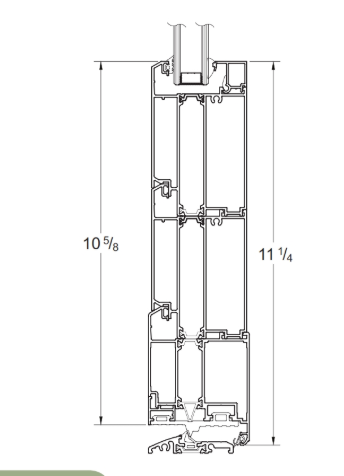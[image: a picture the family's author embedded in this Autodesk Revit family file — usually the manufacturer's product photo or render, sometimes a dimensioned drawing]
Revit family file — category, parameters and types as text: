
# Revit family: Door-Swinging-All_Weather-Series_7000-Nail_On-Outswing_Sidelite
name_source: partatom
category: Doors
units: mm (PartAtom-declared; Revit-internal decimal feet)

## family parameters
Always vertical = Yes
Classification Number = 23.30.10.00
Cut with Voids When Loaded = No
Host = Wall
Room Calculation Point = No
Shared = No

## types (4) — shared parameters
Analytic Construction = <None>
Assembly Code = B2030100
Description = 3 1/4 in frames with mitered corners
Door Width = 3' - 0"
Exterior Trim Finish = Metal-Aluminum-All_Weather-Standard-White
Exterior Trim by others = No
Finish = Metal-Aluminum-All_Weather-Standard-White
Function = Exterior
Glazing = Glass-All_Weather-OA-Insulated_Glass
Height = 8' - 0"
Inset = 0' - 0"
Interior Trim  by others = No
Interior Trim Finish = Metal-Aluminum-All_Weather-Standard-White
Jamb Ext Finish = Metal-Aluminum-All_Weather-Standard-White
Jamb Extensions = No
Manufacturer = All Weather Architectural Aluminum
Max Door Width = 4' - 0"
Max Height = 8' - 0"
Max Sidelite Width = 9' - 5"
Min Door Width = 1' - 10 7/32"
Min Sidelite Width = 1' - 10 7/32"
Model = Outswing Door
Offset = 0' - 0"
Offset Calc = 0' - 0 1/16"
Opening Panel Width = 2' - 4 3/32"
Operation = Swinging
Panel Width = 2' - 7 5/16"
Product Documentation Link = https://28a25771709x0a343azkftap-wpengine.netdna-ssl.com
Product Name = Series 7000
Product Page URL = https://www.allweatheraa.com
Requested Door Width = 3' - 0"
Requested Height = 8' - 0"
Requested Width = 5' - 0"
Rough Height = 8' - 0 1/2"
Rough Width = 5' - 0 3/4"
Sidelite Width = 2' - 0"
Specification = https://28a25771709x0a343azkftap-wpengine.netdna-ssl.com
Thickness = 0' - 3 1/4"
Trim Projection Ext. = 0' - 1"
Trim Projection Int. = 0' - 1"
Trim Width = 0' - 3"
URL = https://www.allweatheraa.com
Wall Closure = By host
Width = 5' - 0"

## per-type parameters (varying)
| type | 10" Kick Plate | 4" Kick Plate | Bottom Glass Offset | Door Bottom Offset | Door Offset InterioR | Low Sill | Standard Sill | Type Comments |
| Outswing with Standard Sill 4" Kick Plate with Sidelite | No | Yes | 0' - 4 23/32" | 0' - 1 3/16" | 0' - 2 3/8" | No | Yes | Outswing Standard Sill 4 in Kick Plate w/ Sidelite |
| Outswing with Low Sill 4" Kick Plate with Sidelite | No | Yes | 0' - 3 13/16" | 0' - 0 1/4" | 0' - 1 21/32" | Yes | No | Outswing Low Sill 4 in Kick Plate w/ Sidelite |
| Outswing with Low Sill 10" Kick Plate with Sidelite | Yes | No | 0' - 11 1/32" | 0' - 0 1/4" | 0' - 1 21/32" | Yes | No | Outswing Low Sill 10 in Kick Plate w/ Sidelite |
| Outswing with Standard Sill 10" Kick Plate with Sidelite | Yes | No | 0' - 11 31/32" | 0' - 1 3/16" | 0' - 2 3/8" | No | Yes | Outswing Standard Sill 10 in Kick Plate w/ Sidelite |

## geometry (parser evidence)
native form markers: Extrusion x3, Sweep x5
no freeform markers — native parametric forms only
